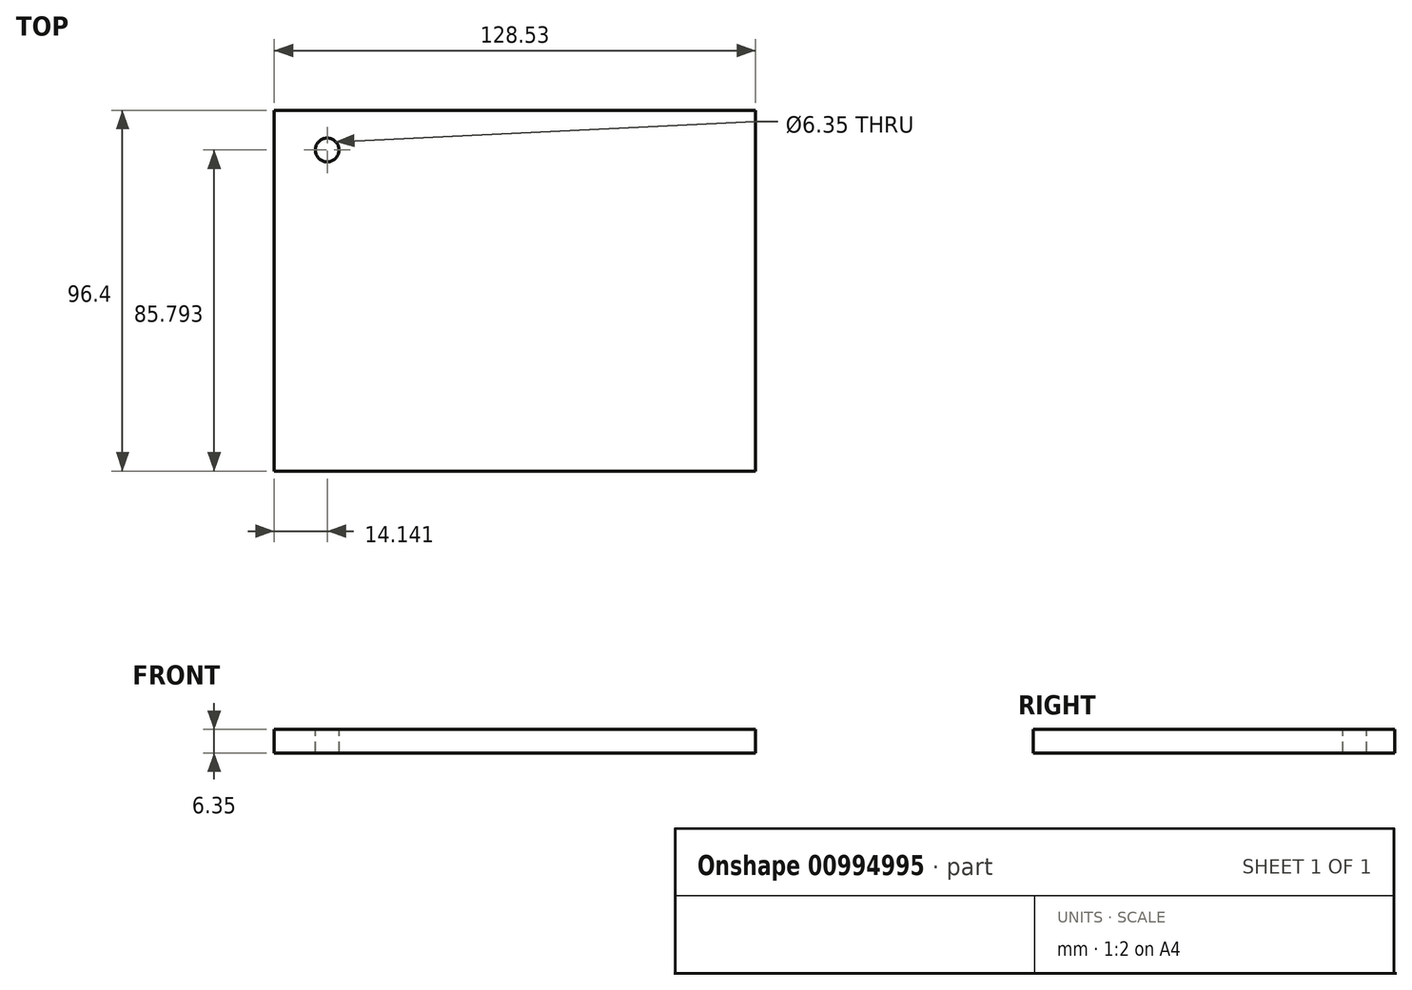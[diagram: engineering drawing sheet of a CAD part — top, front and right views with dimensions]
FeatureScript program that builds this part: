
annotation { "Feature Type Name" : "Feature", "Feature Type Description" : "" }
export const myFeature = defineFeature(function(context is Context, id is Id, definition is map)
    precondition{}
    {
        {
            var Q0;
            Q0=qCreatedBy(makeId("Top.planeOp"),FACE);
            var sketch = newSketch(context, id + "F0", { "sketchPlane" : qUnion([Q0])});
            skLineSegment(sketch, "E0.bottom", {"start": v(-72.14, 47.72) * mm, "end": v(56.4, 47.72) * mm});
            skLineSegment(sketch, "E0.top", {"start": v(-72.14, -48.68) * mm, "end": v(56.4, -48.68) * mm});
            skLineSegment(sketch, "E0.left", {"start": v(-72.14, 47.72) * mm, "end": v(-72.14, -48.68) * mm});
            skLineSegment(sketch, "E0.right", {"start": v(56.4, 47.72) * mm, "end": v(56.4, -48.68) * mm});
            skSolve(sketch);
        }
        {
            var Q0;
            Q0=makeQuery(id+"F0.imprint","IMPRINT",FACE,{"disambiguationData":[TD([[makeQuery(id+"F0.imprint","IMPRINT",EDGE,{"derivedFrom":sQuery(id+"F0.wireOp",EDGE,"E0.bottom")}),-1.0]])]});
            extrude(context, id + "F1", {"entities" : qUnion([Q0]), "depth" : 6.35 * mm, "offsetDistance" : 25.4 * mm});
        }
        {
            var Q0;
            Q0=makeQuery(id+"F1.opExtrude","CAP_FACE",FACE,{"disambiguationData":[OSD([sQuery(id+"F0.wireOp",EDGE,"E0.bottom"),sQuery(id+"F0.wireOp",EDGE,"E0.top"),sQuery(id+"F0.wireOp",EDGE,"E0.left"),sQuery(id+"F0.wireOp",EDGE,"E0.right")])],"isStart":false});
            var sketch = newSketch(context, id + "F2", { "sketchPlane" : qUnion([Q0])});
            skCircle(sketch, "E1", {"center": v(-58, 37.11) * mm, "radius": 5.68 * mm});
            skSolve(sketch);
        }
        {
            var Q0;
            Q0=sQuery(id+"F2.wireOp",VERTEX,"E1.center");
            var Q1;
            Q1=makeQuery(id+"F1.opExtrude","SWEPT_BODY",BODY,{"disambiguationData":[OSD([sQuery(id+"F0.wireOp",EDGE,"E0.bottom"),sQuery(id+"F0.wireOp",EDGE,"E0.top"),sQuery(id+"F0.wireOp",EDGE,"E0.left"),sQuery(id+"F0.wireOp",EDGE,"E0.right")])]});
            hole(context, id + "F3", {"style" : HoleStyle.SIMPLE, "endStyle" : HoleEndStyle.THROUGH, "holeDiameter" : 6.35 * mm, "majorDiameter" : 6.35 * mm, "isTappedThrough" : true, "tappedDepth" : 12.7 * mm, "tapClearance" : 3, "locations" : qUnion([Q0]), "scope" : qUnion([Q1])});
        }
    });
